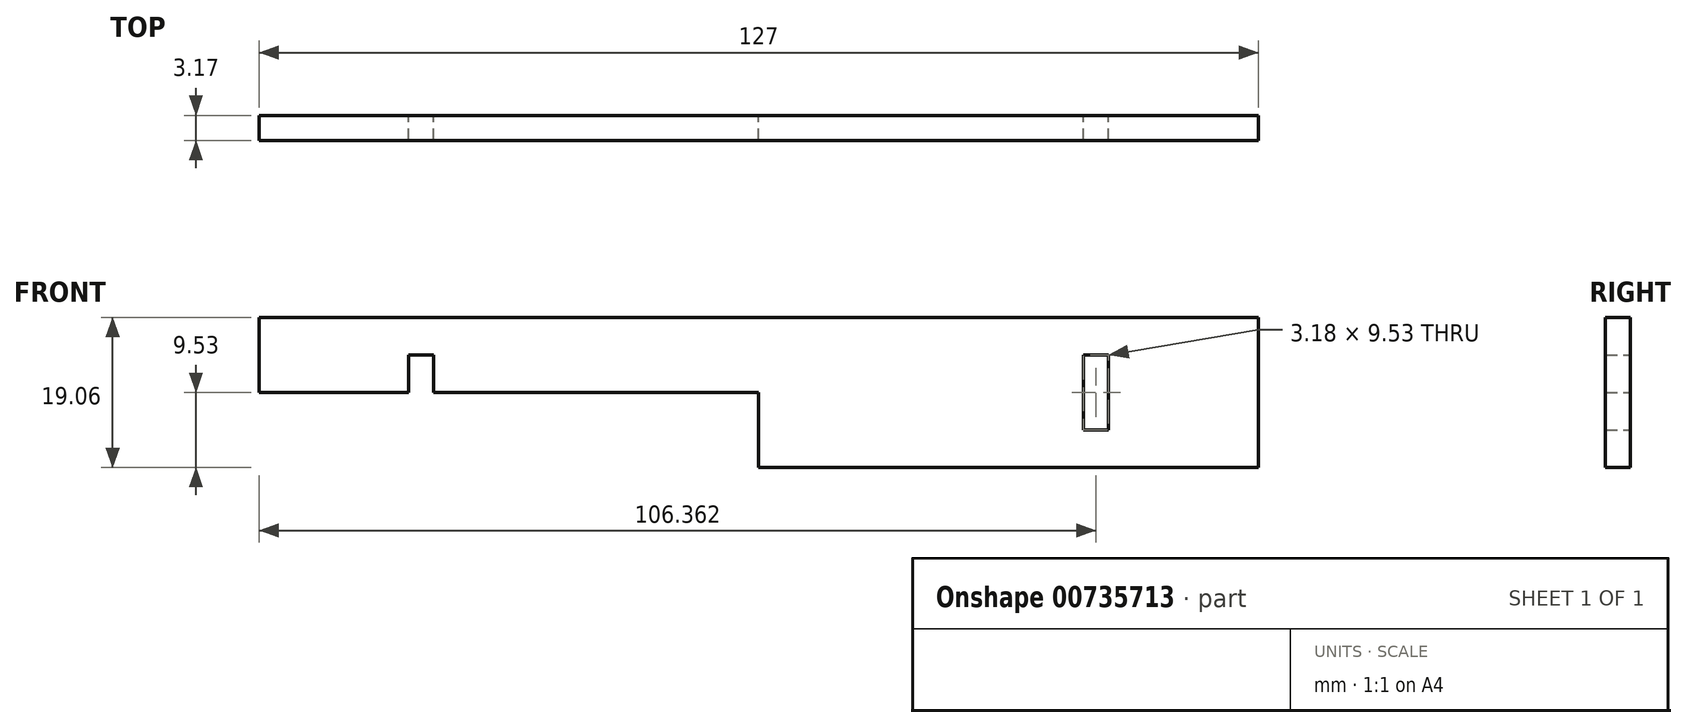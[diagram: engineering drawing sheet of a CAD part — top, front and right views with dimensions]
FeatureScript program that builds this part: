
annotation { "Feature Type Name" : "Feature", "Feature Type Description" : "" }
export const myFeature = defineFeature(function(context is Context, id is Id, definition is map)
    precondition{}
    {
        {
            var Q0;
            Q0=qCreatedBy(makeId("Front.planeOp"),FACE);
            var sketch = newSketch(context, id + "F0", { "sketchPlane" : qUnion([Q0])});
            skLineSegment(sketch, "E0", {"start": v(-63.5, 0) * mm, "end": v(0, 0) * mm});
            skLineSegment(sketch, "E1", {"start": v(0, 0) * mm, "end": v(63.5, 0) * mm});
            skLineSegment(sketch, "E2", {"start": v(63.5, 0) * mm, "end": v(63.5, -9.52) * mm});
            skLineSegment(sketch, "E3", {"start": v(63.5, -9.52) * mm, "end": v(63.5, 9.53) * mm});
            skLineSegment(sketch, "E4", {"start": v(63.5, 9.53) * mm, "end": v(-63.5, 9.53) * mm});
            skLineSegment(sketch, "E5", {"start": v(-63.5, 9.53) * mm, "end": v(-63.5, -9.52) * mm});
            skLineSegment(sketch, "E6", {"start": v(-63.5, -9.52) * mm, "end": v(63.5, -9.52) * mm});
            skLineSegment(sketch, "E7", {"start": v(-63.5, 0) * mm, "end": v(-63.5, 9.53) * mm});
            skLineSegment(sketch, "E8", {"start": v(-63.5, -9.52) * mm, "end": v(-63.5, 0) * mm});
            skLineSegment(sketch, "E9", {"start": v(-44.45, -4.76) * mm, "end": v(-44.45, 4.76) * mm});
            skLineSegment(sketch, "E10", {"start": v(-44.45, 4.76) * mm, "end": v(-41.28, 4.76) * mm});
            skLineSegment(sketch, "E11", {"start": v(-41.28, 4.76) * mm, "end": v(-41.28, -4.76) * mm});
            skLineSegment(sketch, "E12", {"start": v(-41.28, -4.76) * mm, "end": v(-44.45, -4.76) * mm});
            skLineSegment(sketch, "E13", {"start": v(0, 0) * mm, "end": v(0, -9.52) * mm});
            skLineSegment(sketch, "E14.MirrorCS", {"start": v(44.45, -4.76) * mm, "end": v(44.45, 4.76) * mm});
            skLineSegment(sketch, "E15.MirrorCS", {"start": v(41.28, 4.76) * mm, "end": v(41.28, -4.76) * mm});
            skLineSegment(sketch, "E16.MirrorCS", {"start": v(44.45, 4.76) * mm, "end": v(41.28, 4.76) * mm});
            skLineSegment(sketch, "E17.MirrorCS", {"start": v(41.28, -4.76) * mm, "end": v(44.45, -4.76) * mm});
            skSolve(sketch);
        }
        {
            var Q0;
            {var subQ1=sQuery(id+"F0.wireOp",EDGE,"E4");Q0=makeQuery(id+"F0.imprint","IMPRINT",FACE,{"disambiguationData":[TD([[makeQuery(id+"F0.imprint","IMPRINT",EDGE,{"derivedFrom":subQ1}),1.0]])]});}
            var Q1;
            {var subQ0=sQuery(id+"F0.wireOp",EDGE,"E8");Q1=makeQuery(id+"F0.imprint","IMPRINT",FACE,{"disambiguationData":[TD([[makeQuery(id+"F0.imprint","IMPRINT",EDGE,{"derivedFrom":subQ0}),-1.0]])]});}
            var Q2;
            {var subQ5=sQuery(id+"F0.wireOp",EDGE,"E13");Q2=makeQuery(id+"F0.imprint","IMPRINT",FACE,{"disambiguationData":[TD([[makeQuery(id+"F0.imprint","IMPRINT",EDGE,{"derivedFrom":subQ5}),1.0]])]});}
            extrude(context, id + "F1", {"entities" : qUnion([Q0, Q1, Q2]), "depth" : 3.17 * mm, "offsetDistance" : 25.4 * mm});
        }
    });
